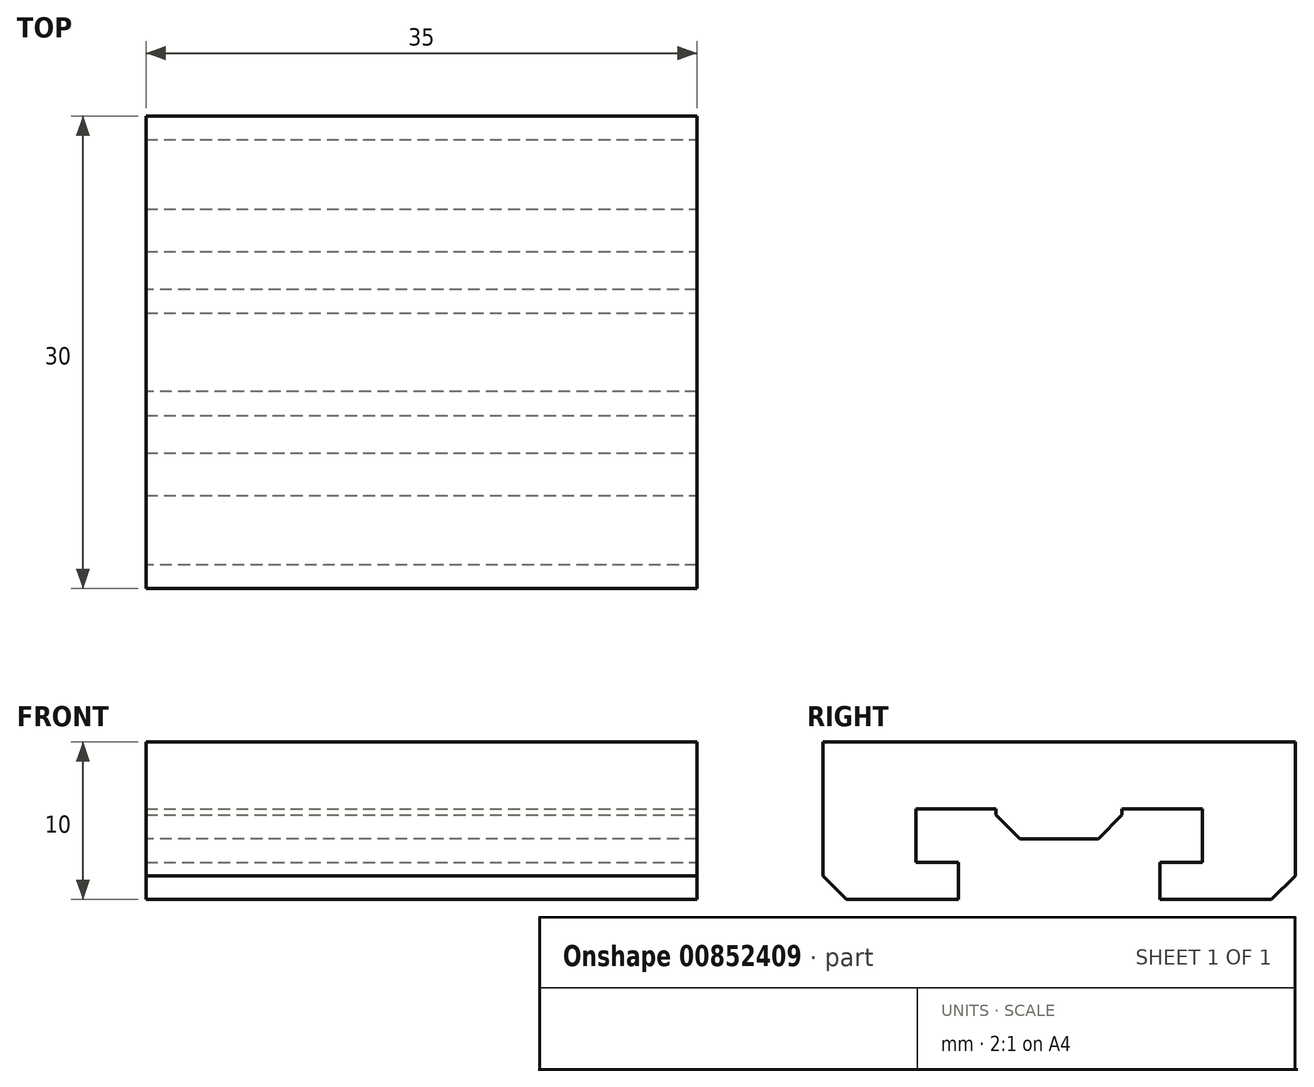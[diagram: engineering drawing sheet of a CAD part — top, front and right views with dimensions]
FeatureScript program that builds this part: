
annotation { "Feature Type Name" : "Feature", "Feature Type Description" : "" }
export const myFeature = defineFeature(function(context is Context, id is Id, definition is map)
    precondition{}
    {
        {
            var Q0;
            Q0=qCreatedBy(makeId("Right.planeOp"),FACE);
            var sketch = newSketch(context, id + "F0", { "sketchPlane" : qUnion([Q0])});
            skLineSegment(sketch, "E0.bottom", {"start": v(29.06, -26.8) * mm, "end": v(43.56, -26.8) * mm});
            skLineSegment(sketch, "E0.top", {"start": v(29.06, -36.8) * mm, "end": v(59.06, -36.8) * mm});
            skLineSegment(sketch, "E0.left", {"start": v(29.06, -26.8) * mm, "end": v(29.06, -36.8) * mm});
            skLineSegment(sketch, "E0.right", {"start": v(59.06, -26.8) * mm, "end": v(59.06, -36.8) * mm});
            skPoint(sketch, "E1", {"position": v(44.06, -36.8) * mm});
            skLineSegment(sketch, "E2.top", {"start": v(37.66, -36.8) * mm, "end": v(50.46, -36.8) * mm});
            skLineSegment(sketch, "E2.left", {"start": v(37.66, -34.46) * mm, "end": v(37.66, -36.8) * mm});
            skLineSegment(sketch, "E2.right", {"start": v(50.46, -34.46) * mm, "end": v(50.46, -36.8) * mm});
            skLineSegment(sketch, "E3.bottom", {"start": v(34.96, -31.06) * mm, "end": v(40.06, -31.06) * mm});
            skLineSegment(sketch, "E3.top", {"start": v(34.96, -34.46) * mm, "end": v(37.66, -34.46) * mm});
            skLineSegment(sketch, "E3.left", {"start": v(34.96, -31.06) * mm, "end": v(34.96, -34.46) * mm});
            skLineSegment(sketch, "E3.right", {"start": v(53.16, -31.06) * mm, "end": v(53.16, -34.46) * mm});
            skPoint(sketch, "E4", {"position": v(44.06, -31.06) * mm});
            skPoint(sketch, "E5", {"position": v(40.06, -31.06) * mm});
            skPoint(sketch, "E6", {"position": v(48.06, -31.06) * mm});
            skPoint(sketch, "E7", {"position": v(34.96, -32.96) * mm});
            skLineSegment(sketch, "E8.top", {"start": v(48.06, -32.96) * mm, "end": v(40.06, -32.96) * mm});
            skLineSegment(sketch, "E8.left", {"start": v(48.06, -31.06) * mm, "end": v(48.06, -32.96) * mm});
            skLineSegment(sketch, "E8.right", {"start": v(40.06, -31.06) * mm, "end": v(40.06, -32.96) * mm});
            skLineSegment(sketch, "E9.trimOffspring", {"start": v(48.06, -31.06) * mm, "end": v(53.16, -31.06) * mm});
            skLineSegment(sketch, "E10.trimOffspring", {"start": v(50.46, -34.46) * mm, "end": v(53.16, -34.46) * mm});
            skLineSegment(sketch, "E11.trimOffspring", {"start": v(44.56, -26.8) * mm, "end": v(59.06, -26.8) * mm});
            skPoint(sketch, "E12.left.start.orphan", {"position": v(44.06, -26.8) * mm});
            skLineSegment(sketch, "E13", {"start": v(43.56, -26.8) * mm, "end": v(44.56, -26.8) * mm});
            skSolve(sketch);
        }
        {
            var Q0;
            Q0=makeQuery(id+"F0.imprint","IMPRINT",FACE,{"disambiguationData":[TD([[makeQuery(id+"F0.imprint","IMPRINT",EDGE,{"derivedFrom":sQuery(id+"F0.wireOp",EDGE,"E0.bottom")}),-1.0]])]});
            extrude(context, id + "F1", {"entities" : qUnion([Q0]), "oppositeDirection" : true, "depth" : 35 * mm, "offsetDistance" : 25 * mm});
        }
        {
            var Q0;
            Q0=makeQuery(id+"F1.opExtrude","SWEPT_EDGE",EDGE,{"disambiguationData":[OSD([sQuery(id+"F0.wireOp",EDGE,"E0.top"),sQuery(id+"F0.wireOp",EDGE,"E0.right")])]});
            var Q1;
            Q1=makeQuery(id+"F1.opExtrude","SWEPT_EDGE",EDGE,{"disambiguationData":[OSD([sQuery(id+"F0.wireOp",EDGE,"E8.top"),sQuery(id+"F0.wireOp",EDGE,"E8.left")])]});
            var Q2;
            Q2=makeQuery(id+"F1.opExtrude","SWEPT_EDGE",EDGE,{"disambiguationData":[OSD([sQuery(id+"F0.wireOp",EDGE,"E8.top"),sQuery(id+"F0.wireOp",EDGE,"E8.right")])]});
            var Q3;
            Q3=makeQuery(id+"F1.opExtrude","SWEPT_EDGE",EDGE,{"disambiguationData":[OSD([sQuery(id+"F0.wireOp",EDGE,"E0.top"),sQuery(id+"F0.wireOp",EDGE,"E0.left")])]});
            chamfer(context, id + "F2", {"entities" : qUnion([Q0, Q1, Q2, Q3]), "width" : 1.5 * mm, "tangentPropagation" : true});
        }
    });
